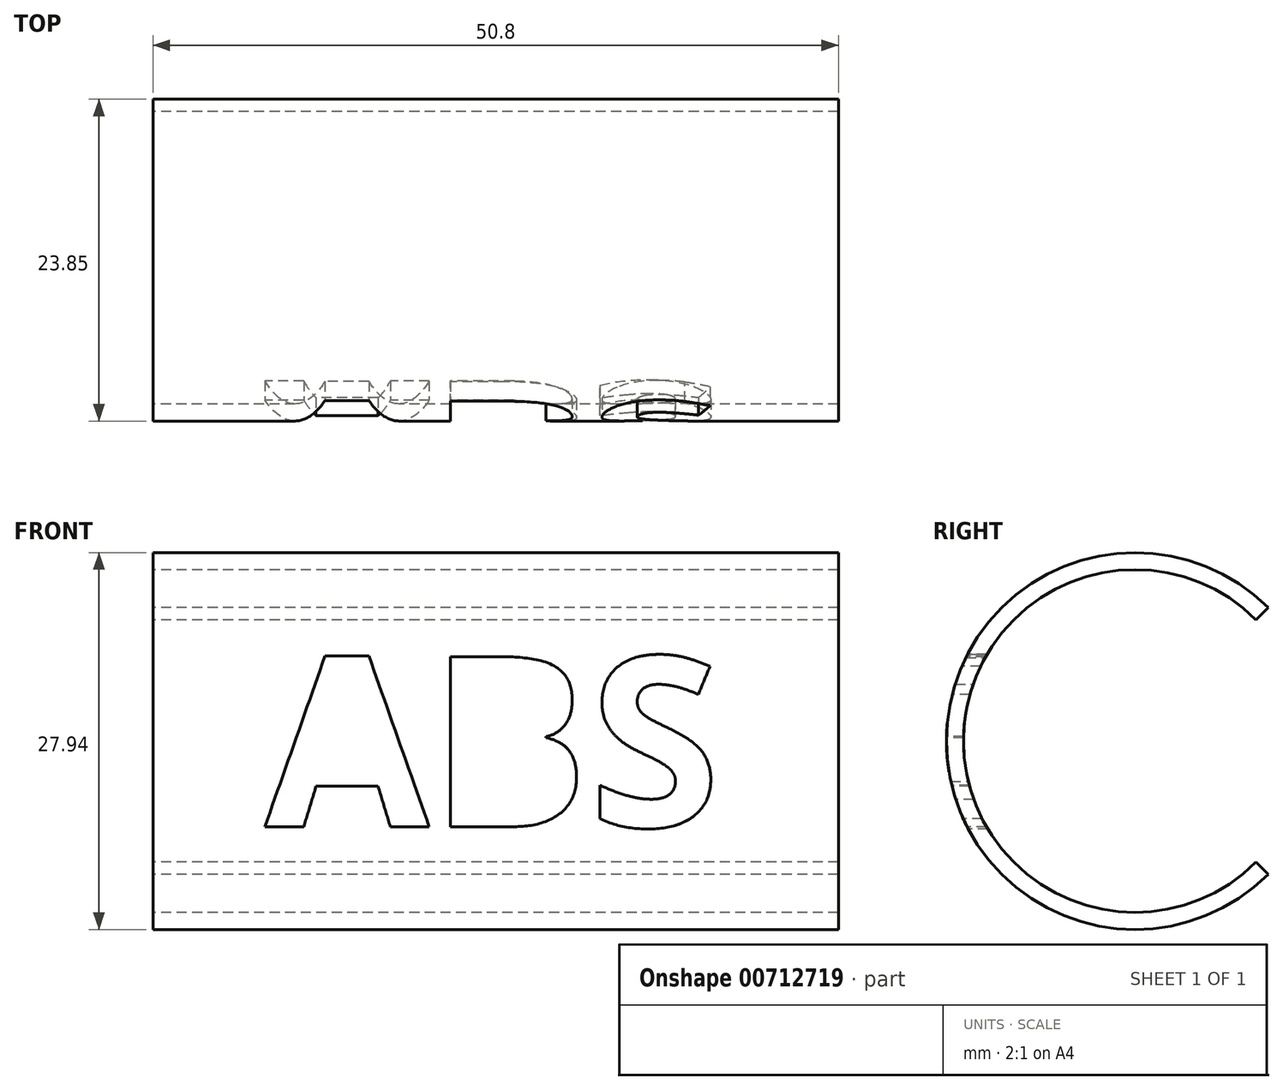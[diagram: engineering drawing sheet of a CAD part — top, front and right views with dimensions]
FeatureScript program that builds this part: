
annotation { "Feature Type Name" : "Feature", "Feature Type Description" : "" }
export const myFeature = defineFeature(function(context is Context, id is Id, definition is map)
    precondition{}
    {
        {
            var Q0;
            Q0=qCreatedBy(makeId("Right.planeOp"),FACE);
            var sketch = newSketch(context, id + "F0", { "sketchPlane" : qUnion([Q0])});
            skCircle(sketch, "E0", {"center": v(0, 0) * mm, "radius": 12.7 * mm});
            skCircle(sketch, "E1", {"center": v(0, 0) * mm, "radius": 13.97 * mm});
            skLineSegment(sketch, "E2", {"start": v(0, 0) * mm, "end": v(13.97, 0) * mm});
            skLineSegment(sketch, "E3", {"start": v(0, 0) * mm, "end": v(9.88, 9.88) * mm});
            skLineSegment(sketch, "E4.MirrorCS", {"start": v(0, 0) * mm, "end": v(9.88, -9.88) * mm});
            skSolve(sketch);
        }
        {
            var Q0;
            {var subQ0=sQuery(id+"F0.wireOp",EDGE,"E3");var subQ1=sQuery(id+"F0.wireOp",EDGE,"E0");var subQ2=makeQuery(id+"F0.imprint","INTERSECT",VERTEX,{"derivedFrom":[subQ1,subQ0]});Q0=makeQuery(id+"F0.imprint","IMPRINT",FACE,{"disambiguationData":[TD([[makeQuery(id+"F0.imprint","IMPRINT",EDGE,{"disambiguationData":[TD([[subQ2,-1.0]])],"derivedFrom":subQ1}),-1.0]])]});}
            extrude(context, id + "F1", {"entities" : qUnion([Q0]), "depth" : 50.8 * mm, "offsetDistance" : 25.4 * mm});
        }
        {
            var Q0;
            Q0=qCreatedBy(makeId("Front.planeOp"),FACE);
            cPlane(context, id + "F2", {"entities" : qUnion([Q0]), "cplaneType" : CPlaneType.OFFSET, "offset" : 25.4 * mm, "width" : 152.4 * mm, "height" : 152.4 * mm});
        }
        {
            var Q0;
            Q0=qCreatedBy(id+"F2.planeOp",FACE);
            var sketch = newSketch(context, id + "F3", { "sketchPlane" : qUnion([Q0])});
            skLineSegment(sketch, "E5.bottom", {"start": v(0, 13.97) * mm, "end": v(50.8, 13.97) * mm});
            skLineSegment(sketch, "E5.top", {"start": v(0, -13.97) * mm, "end": v(50.8, -13.97) * mm});
            skLineSegment(sketch, "E5.left", {"start": v(0, 13.97) * mm, "end": v(0, -13.97) * mm});
            skLineSegment(sketch, "E5.right", {"start": v(50.8, 13.97) * mm, "end": v(50.8, -13.97) * mm});
            skPoint(sketch, "E6", {"position": v(25.4, 13.97) * mm});
            skText(sketch, "E7", { "text": "ABS", "fontName": "OpenSans-Bold.ttf"});
            const initialGuessF3  = {"E7": [0.0083, -0.00635, 1, 0, 0.0127]};
            skSetInitialGuess(sketch, initialGuessF3);
            skSolve(sketch);
        }
        {
            var Q0;
            Q0=makeQuery(id+"F3.imprint","IMPRINT",FACE,{"disambiguationData":[TD([[makeQuery(id+"F3.imprint","IMPRINT",EDGE,{"derivedFrom":sQuery(id+"F3.wireOp",EDGE,"E7.sketch_text.stroke-37")}),-1.0]])]});
            var Q1;
            Q1=makeQuery(id+"F3.imprint","IMPRINT",FACE,{"disambiguationData":[TD([[makeQuery(id+"F3.imprint","IMPRINT",EDGE,{"derivedFrom":sQuery(id+"F3.wireOp",EDGE,"E7.sketch_text.stroke-12")}),-1.0]])]});
            var Q2;
            Q2=makeQuery(id+"F3.imprint","IMPRINT",FACE,{"disambiguationData":[TD([[makeQuery(id+"F3.imprint","IMPRINT",EDGE,{"derivedFrom":sQuery(id+"F3.wireOp",EDGE,"E7.sketch_text.stroke-31")}),1.0]])]});
            var Q3;
            Q3=makeQuery(id+"F3.imprint","IMPRINT",FACE,{"disambiguationData":[TD([[makeQuery(id+"F3.imprint","IMPRINT",EDGE,{"derivedFrom":sQuery(id+"F3.wireOp",EDGE,"E7.sketch_text.stroke-24")}),1.0]])]});
            var Q4;
            Q4=makeQuery(id+"F3.imprint","IMPRINT",FACE,{"disambiguationData":[TD([[makeQuery(id+"F3.imprint","IMPRINT",EDGE,{"derivedFrom":sQuery(id+"F3.wireOp",EDGE,"E7.sketch_text.stroke-0")}),-1.0]])]});
            var Q5;
            Q5=makeQuery(id+"F3.imprint","IMPRINT",FACE,{"disambiguationData":[TD([[makeQuery(id+"F3.imprint","IMPRINT",EDGE,{"derivedFrom":sQuery(id+"F3.wireOp",EDGE,"E7.sketch_text.stroke-8")}),1.0]])]});
            extrude(context, id + "F4", {"entities" : qUnion([Q0, Q1, Q2, Q3, Q4, Q5]), "operationType" : NewBodyOperationType.REMOVE, "endBound" : BoundingType.THROUGH_ALL, "oppositeDirection" : true, "depth" : 25.4 * mm, "offsetDistance" : 25.4 * mm});
        }
    });
